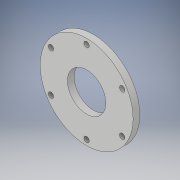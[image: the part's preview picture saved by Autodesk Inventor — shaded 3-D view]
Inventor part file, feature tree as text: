
AUTODESK INVENTOR PART (.ipt)
format: ipt  version: 2017 (Build 210142000, 142)  size: 118,272 bytes
history: native  units: in
note: dims shown in document units (in); Inventor stores cm internally (conversion verified against a paired STEP export)
features: extrude x3, sketch x3
ambient origin geometry x8: Origin, YZ Plane, XZ Plane, XY Plane, X Axis, Y Axis, Z Axis, Center Point
bodies: Solid1 (feature_tree)
feature tree (6):
  extrude  "Extrusion1"  Depth=0.235in TaperAngle=0.0deg
  extrude  "Extrusion2"  Depth=0.235in TaperAngle=0.0deg
  extrude  "Extrusion3"  Depth=0.235in TaperAngle=360.0deg
  sketch  "Sketch1"  dims[d0=3.24in d1=0.235in d2=0.0in]
  sketch  "Sketch2"  dims[d3=1.34in d4=0.235in d5=0.0in]
  sketch  "Sketch3"  dims[d6=0.1875in d7=2.3622in d9=360.0deg d11=0.235in d12=0.0in]
